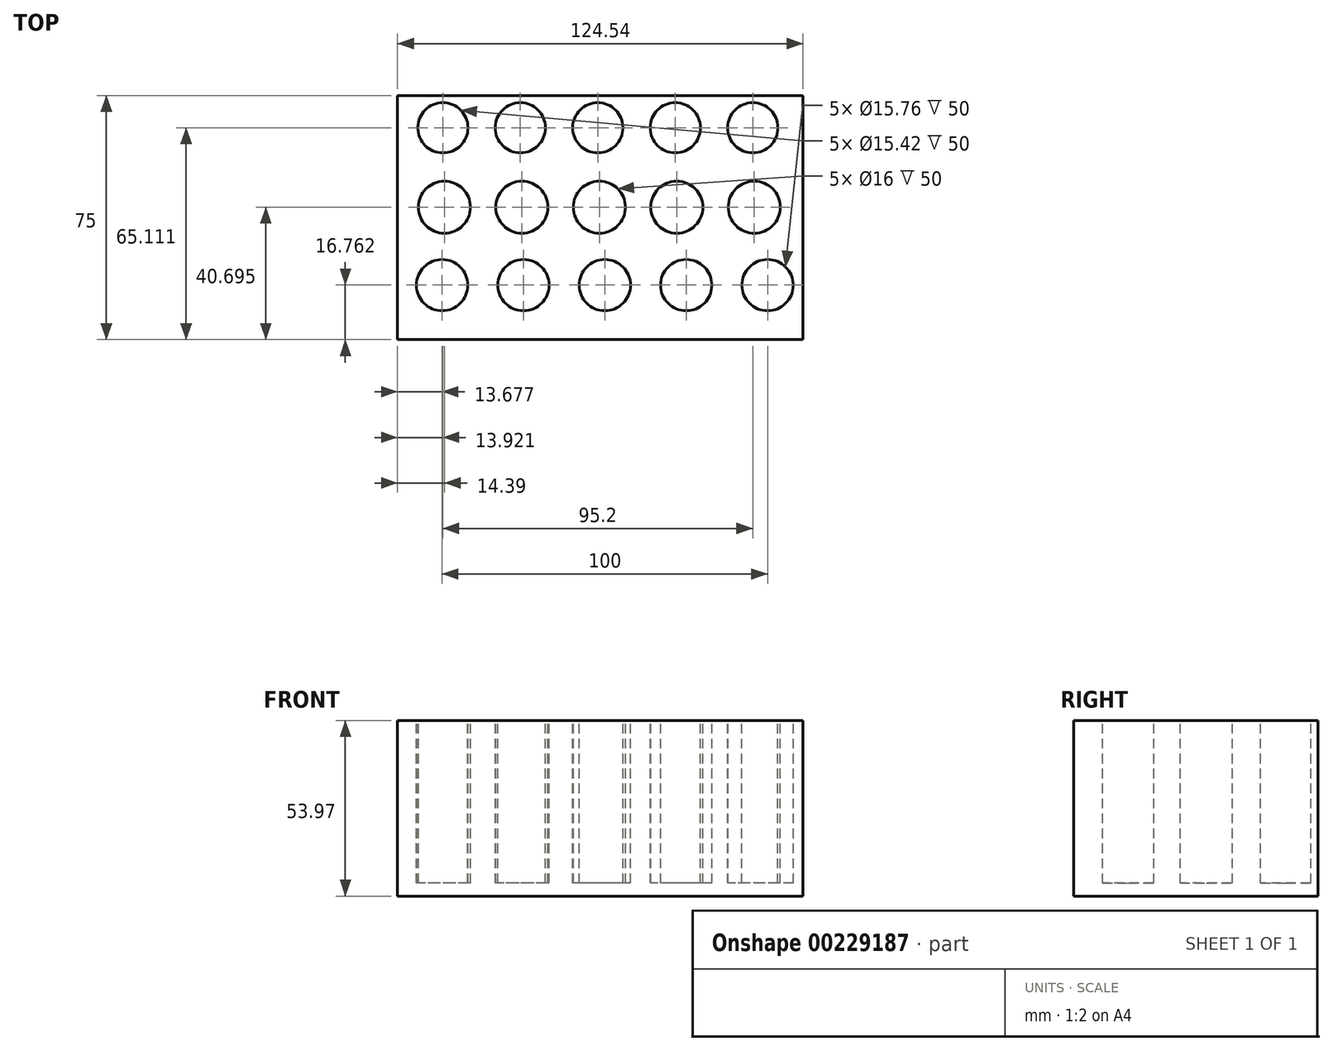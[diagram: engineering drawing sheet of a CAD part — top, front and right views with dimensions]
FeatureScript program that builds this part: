
annotation { "Feature Type Name" : "Feature", "Feature Type Description" : "" }
export const myFeature = defineFeature(function(context is Context, id is Id, definition is map)
    precondition{}
    {
        {
            var Q0;
            Q0=qCreatedBy(makeId("Front.planeOp"),FACE);
            var sketch = newSketch(context, id + "F0", { "sketchPlane" : qUnion([Q0])});
            skLineSegment(sketch, "E0.bottom", {"start": v(-62.27, 26.74) * mm, "end": v(62.27, 26.74) * mm});
            skLineSegment(sketch, "E0.top", {"start": v(-62.27, -27.23) * mm, "end": v(62.27, -27.23) * mm});
            skLineSegment(sketch, "E0.left", {"start": v(-62.27, 26.74) * mm, "end": v(-62.27, -27.23) * mm});
            skLineSegment(sketch, "E0.right", {"start": v(62.27, 26.74) * mm, "end": v(62.27, -27.23) * mm});
            skSolve(sketch);
        }
        {
            var Q0;
            Q0=makeQuery(id+"F0.imprint","IMPRINT",FACE,{"disambiguationData":[TD([[makeQuery(id+"F0.imprint","IMPRINT",EDGE,{"derivedFrom":sQuery(id+"F0.wireOp",EDGE,"E0.bottom")}),-1.0]])]});
            extrude(context, id + "F1", {"entities" : qUnion([Q0]), "depth" : 75 * mm});
        }
        {
            var Q0;
            Q0=makeQuery(id+"F1.opExtrude","SWEPT_FACE",FACE,{"disambiguationData":[OSD([sQuery(id+"F0.wireOp",EDGE,"E0.bottom")])]});
            var sketch = newSketch(context, id + "F2", { "sketchPlane" : qUnion([Q0])});
            skCircle(sketch, "E1", {"center": v(-48.35, -9.89) * mm, "radius": 7.71 * mm});
            skCircle(sketch, "E2.1.0.0", {"center": v(-24.55, -9.89) * mm, "radius": 7.71 * mm});
            skCircle(sketch, "E2.2.0.0", {"center": v(-0.75, -9.89) * mm, "radius": 7.71 * mm});
            skLineSegment(sketch, "E2.direction1", {"start": v(-48.35, -9.89) * mm, "end": v(-24.55, -9.89) * mm, "construction": true});
            skCircle(sketch, "E3.0.3.0", {"center": v(23.05, -9.89) * mm, "radius": 7.71 * mm});
            skCircle(sketch, "E3.0.4.0", {"center": v(46.85, -9.89) * mm, "radius": 7.71 * mm});
            skSolve(sketch);
        }
        {
            var Q0;
            Q0=makeQuery(id+"F2.imprint","IMPRINT",FACE,{"disambiguationData":[TD([[makeQuery(id+"F2.imprint","IMPRINT",EDGE,{"derivedFrom":sQuery(id+"F2.wireOp",EDGE,"E1")}),-1.0]])]});
            var sketch = newSketch(context, id + "F3", { "sketchPlane" : qUnion([Q0])});
            skCircle(sketch, "E4", {"center": v(-47.88, -34.3) * mm, "radius": 8 * mm});
            skCircle(sketch, "E5.1.0.0", {"center": v(-24.08, -34.3) * mm, "radius": 8 * mm});
            skCircle(sketch, "E5.2.0.0", {"center": v(-0.28, -34.3) * mm, "radius": 8 * mm});
            skLineSegment(sketch, "E5.direction1", {"start": v(-47.88, -34.3) * mm, "end": v(-24.08, -34.3) * mm, "construction": true});
            skCircle(sketch, "E6.0.3.0", {"center": v(23.52, -34.3) * mm, "radius": 8 * mm});
            skCircle(sketch, "E6.0.4.0", {"center": v(47.32, -34.3) * mm, "radius": 8 * mm});
            skSolve(sketch);
        }
        {
            var Q0;
            Q0=makeQuery(id+"F2.imprint","IMPRINT",FACE,{"disambiguationData":[TD([[makeQuery(id+"F2.imprint","IMPRINT",EDGE,{"derivedFrom":sQuery(id+"F2.wireOp",EDGE,"E1")}),-1.0]])]});
            var sketch = newSketch(context, id + "F4", { "sketchPlane" : qUnion([Q0])});
            skCircle(sketch, "E7", {"center": v(-48.6, -58.24) * mm, "radius": 7.88 * mm});
            skCircle(sketch, "E8.1.0.0", {"center": v(-23.6, -58.24) * mm, "radius": 7.88 * mm});
            skCircle(sketch, "E8.2.0.0", {"center": v(1.4, -58.24) * mm, "radius": 7.88 * mm});
            skLineSegment(sketch, "E8.direction1", {"start": v(-48.6, -58.24) * mm, "end": v(-23.6, -58.24) * mm, "construction": true});
            skCircle(sketch, "E9.0.3.0", {"center": v(26.4, -58.24) * mm, "radius": 7.88 * mm});
            skCircle(sketch, "E9.0.4.0", {"center": v(51.4, -58.24) * mm, "radius": 7.88 * mm});
            skSolve(sketch);
        }
        {
            var Q0;
            Q0 = qSketchRegion(id + "F4", true);
            var Q1;
            Q1 = qSketchRegion(id + "F3", true);
            var Q2;
            Q2 = qSketchRegion(id + "F2", true);
            extrude(context, id + "F5", {"entities" : qUnion([Q0, Q1, Q2]), "operationType" : NewBodyOperationType.REMOVE, "oppositeDirection" : true, "depth" : 50 * mm});
        }
    });
